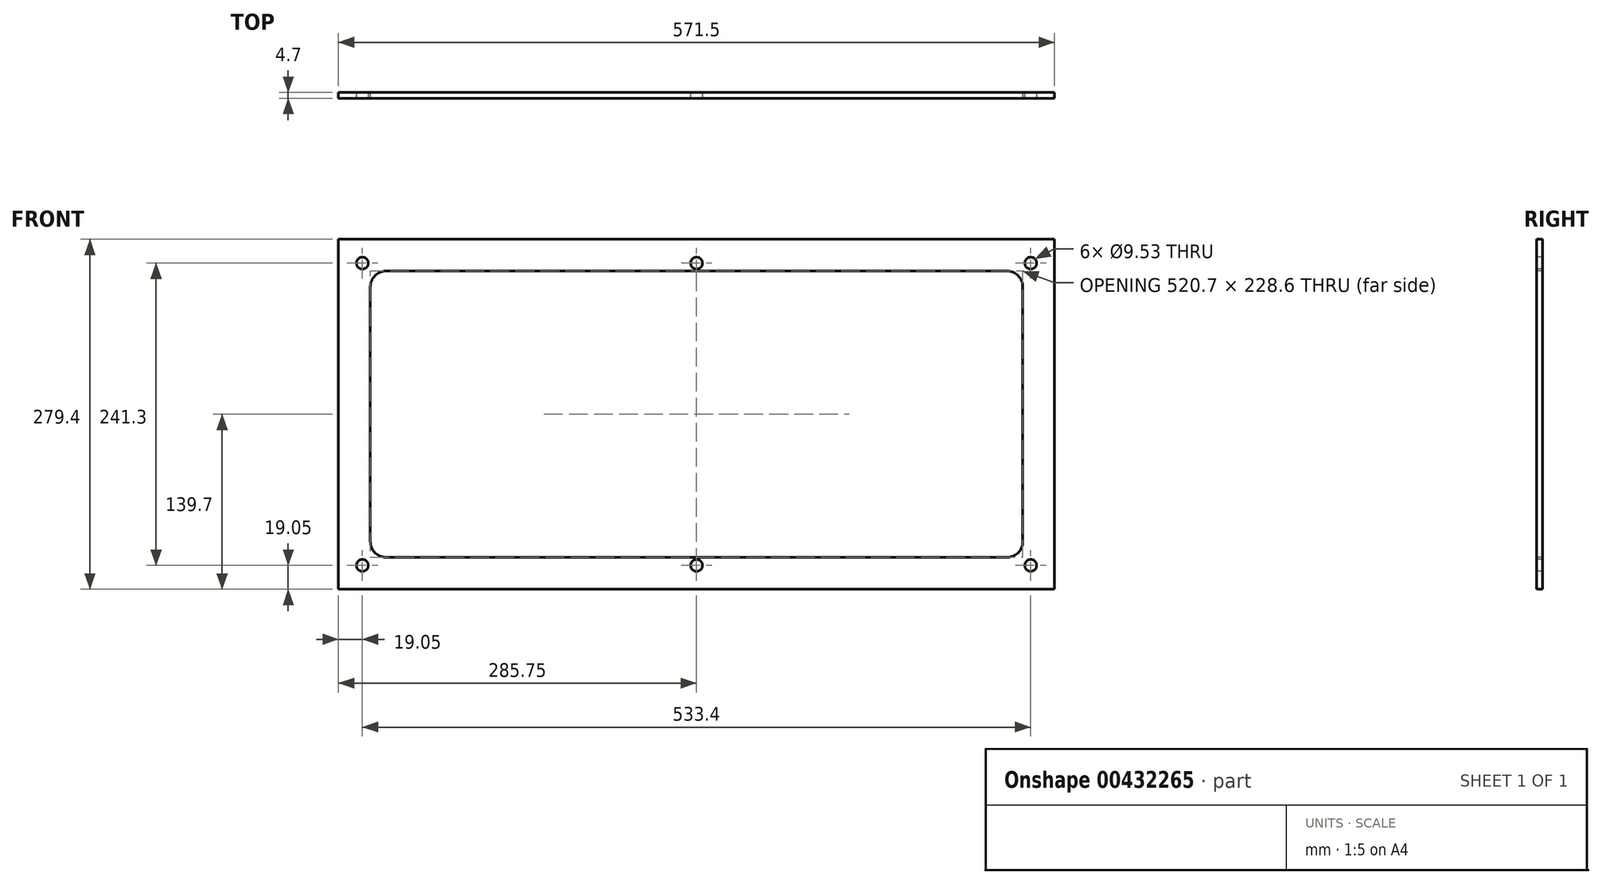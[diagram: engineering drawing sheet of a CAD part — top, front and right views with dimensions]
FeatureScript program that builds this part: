
annotation { "Feature Type Name" : "Feature", "Feature Type Description" : "" }
export const myFeature = defineFeature(function(context is Context, id is Id, definition is map)
    precondition{}
    {
        {
            var Q0;
            Q0=qCreatedBy(makeId("Front.planeOp"),FACE);
            var sketch = newSketch(context, id + "F0", { "sketchPlane" : qUnion([Q0])});
            skLineSegment(sketch, "E0.bottom", {"start": v(-285.75, 139.7) * mm, "end": v(285.75, 139.7) * mm});
            skLineSegment(sketch, "E0.top", {"start": v(-285.75, -139.7) * mm, "end": v(285.75, -139.7) * mm});
            skLineSegment(sketch, "E0.left", {"start": v(-285.75, 139.7) * mm, "end": v(-285.75, -139.7) * mm});
            skLineSegment(sketch, "E0.right", {"start": v(285.75, 139.7) * mm, "end": v(285.75, -139.7) * mm});
            skPoint(sketch, "E0.middle", {"position": v(0, 0) * mm});
            skSolve(sketch);
        }
        {
            var Q0;
            Q0=qSketchRegion(id+"F0",true);
            extrude(context, id + "F1", {"entities" : qUnion([Q0]), "depth" : 4.7 * mm, "offsetDistance" : 25.4 * mm});
        }
        {
            var Q0;
            Q0=makeQuery(id+"F1.opExtrude","CAP_FACE",FACE,{"disambiguationData":[OSD([sQuery(id+"F0.wireOp",EDGE,"E0.bottom"),sQuery(id+"F0.wireOp",EDGE,"E0.top"),sQuery(id+"F0.wireOp",EDGE,"E0.left"),sQuery(id+"F0.wireOp",EDGE,"E0.right")])],"isStart":false});
            var sketch = newSketch(context, id + "F2", { "sketchPlane" : qUnion([Q0])});
            skLineSegment(sketch, "E1.bottom", {"start": v(-247.65, 114.3) * mm, "end": v(247.65, 114.3) * mm});
            skLineSegment(sketch, "E1.top", {"start": v(-247.65, -114.3) * mm, "end": v(247.65, -114.3) * mm});
            skLineSegment(sketch, "E1.left", {"start": v(-260.35, 101.6) * mm, "end": v(-260.35, -101.6) * mm});
            skLineSegment(sketch, "E1.right", {"start": v(260.35, 101.6) * mm, "end": v(260.35, -101.6) * mm});
            skPoint(sketch, "E1.middle", {"position": v(0, 0) * mm});
            skPoint(sketch, "E2.visualSharp", {"position": v(-260.35, 114.3) * mm});
            skArc(sketch, "E2.filletArc", {"start": v(-247.65, 114.3) * mm, "mid": v(-256.63, 110.58) * mm, "end": v(-260.35, 101.6) * mm});
            skPoint(sketch, "E3.visualSharp", {"position": v(-260.35, -114.3) * mm});
            skArc(sketch, "E3.filletArc", {"start": v(-260.35, -101.6) * mm, "mid": v(-256.63, -110.58) * mm, "end": v(-247.65, -114.3) * mm});
            skPoint(sketch, "E4.visualSharp", {"position": v(260.35, 114.3) * mm});
            skArc(sketch, "E4.filletArc", {"start": v(260.35, 101.6) * mm, "mid": v(256.63, 110.58) * mm, "end": v(247.65, 114.3) * mm});
            skPoint(sketch, "E5.visualSharp", {"position": v(260.35, -114.3) * mm});
            skArc(sketch, "E5.filletArc", {"start": v(247.65, -114.3) * mm, "mid": v(256.63, -110.58) * mm, "end": v(260.35, -101.6) * mm});
            skSolve(sketch);
        }
        {
            var Q0;
            Q0 = qSketchRegion(id + "F2", true);
            extrude(context, id + "F3", {"entities" : qUnion([Q0]), "operationType" : NewBodyOperationType.REMOVE, "endBound" : BoundingType.THROUGH_ALL, "oppositeDirection" : true, "depth" : 25.4 * mm, "offsetDistance" : 25.4 * mm});
        }
        {
            var Q0;
            Q0=makeQuery(id+"F1.opExtrude","CAP_FACE",FACE,{"disambiguationData":[OSD([sQuery(id+"F0.wireOp",EDGE,"E0.bottom"),sQuery(id+"F0.wireOp",EDGE,"E0.top"),sQuery(id+"F0.wireOp",EDGE,"E0.left"),sQuery(id+"F0.wireOp",EDGE,"E0.right")])],"isStart":false});
            var sketch = newSketch(context, id + "F4", { "sketchPlane" : qUnion([Q0])});
            skLineSegment(sketch, "E6", {"start": v(0, 163.7) * mm, "end": v(0, -163.75) * mm, "construction": true});
            skPoint(sketch, "E6.endSnap0", {"position": v(0, -139.7) * mm});
            skLineSegment(sketch, "E7", {"start": v(-317, 0) * mm, "end": v(357.16, 0) * mm, "construction": true});
            skLineSegment(sketch, "E8", {"start": v(-228.8, -114.3) * mm, "end": v(-228.8, -123.83) * mm});
            skLineSegment(sketch, "E9", {"start": v(-260.35, -94.43) * mm, "end": v(-269.88, -94.43) * mm});
            skLineSegment(sketch, "E10", {"start": v(239.1, -114.3) * mm, "end": v(239.1, -123.83) * mm});
            skLineSegment(sketch, "E11", {"start": v(260.35, -94.07) * mm, "end": v(269.88, -94.07) * mm});
            skCircle(sketch, "E12", {"center": v(-266.7, -120.65) * mm, "radius": 4.76 * mm});
            skCircle(sketch, "E13", {"center": v(0, -120.65) * mm, "radius": 4.76 * mm});
            skCircle(sketch, "E14", {"center": v(266.7, -120.65) * mm, "radius": 4.76 * mm});
            skCircle(sketch, "E15", {"center": v(266.7, 120.65) * mm, "radius": 4.76 * mm});
            skCircle(sketch, "E16", {"center": v(0, 120.65) * mm, "radius": 4.76 * mm});
            skCircle(sketch, "E17", {"center": v(-266.7, 120.65) * mm, "radius": 4.76 * mm});
            skSolve(sketch);
        }
        {
            var Q0;
            Q0 = qSketchRegion(id + "F4", true);
            extrude(context, id + "F5", {"entities" : qUnion([Q0]), "operationType" : NewBodyOperationType.REMOVE, "endBound" : BoundingType.THROUGH_ALL, "oppositeDirection" : true, "depth" : 25.4 * mm, "offsetDistance" : 25.4 * mm});
        }
    });
